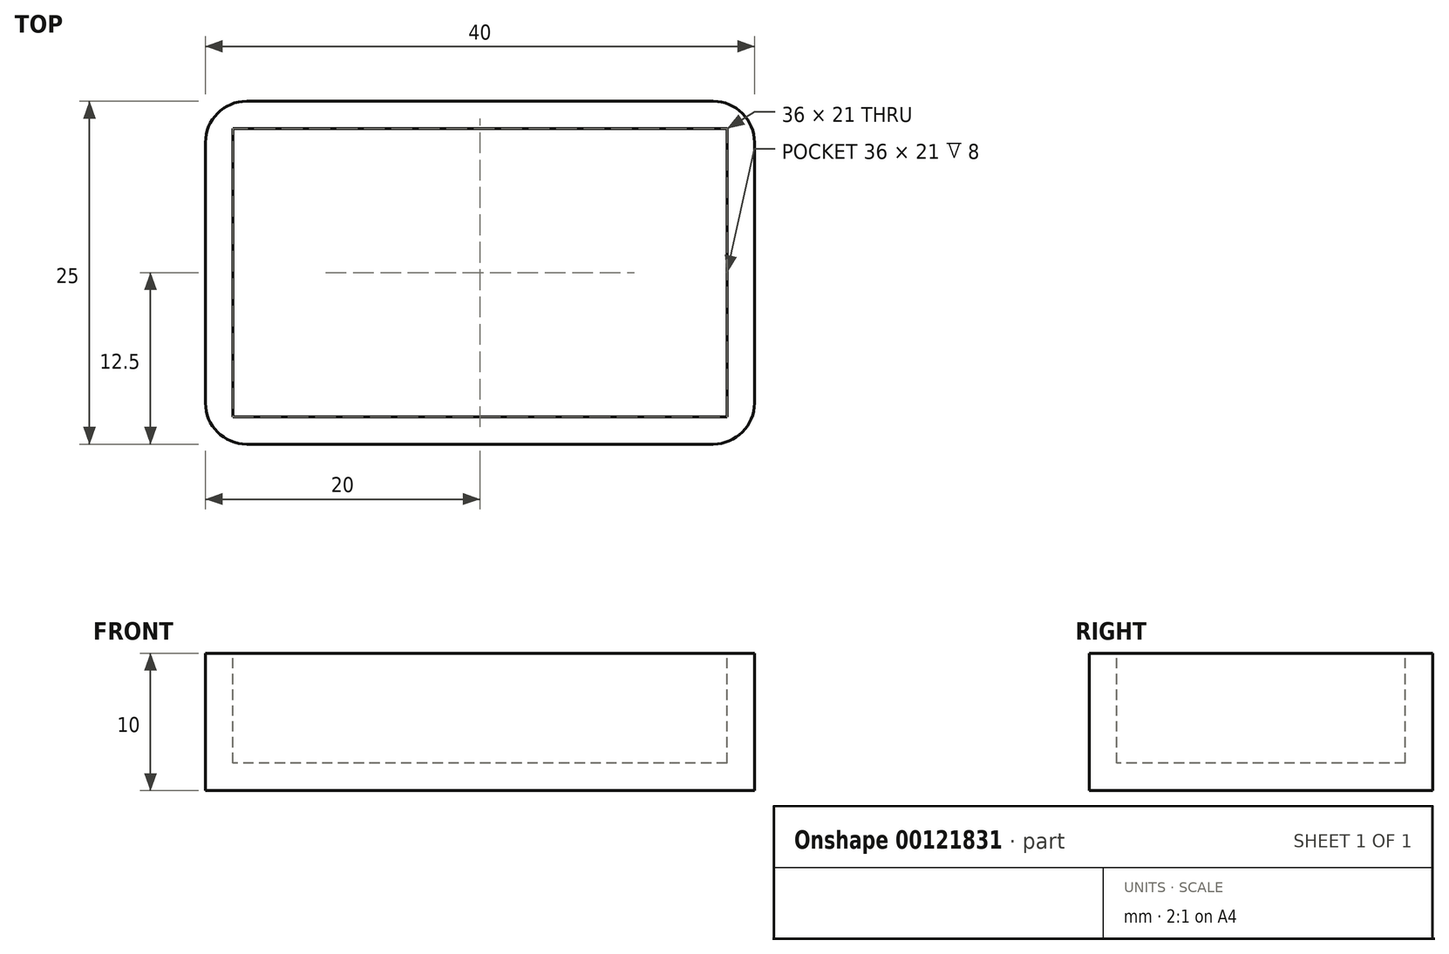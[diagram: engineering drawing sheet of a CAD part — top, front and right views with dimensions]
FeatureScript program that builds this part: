
annotation { "Feature Type Name" : "Feature", "Feature Type Description" : "" }
export const myFeature = defineFeature(function(context is Context, id is Id, definition is map)
    precondition{}
    {
        {
            var Q0;
            Q0=qCreatedBy(makeId("Top.planeOp"),FACE);
            var sketch = newSketch(context, id + "F0", { "sketchPlane" : qUnion([Q0])});
            skLineSegment(sketch, "E0.bottom", {"start": v(20, 12.5) * mm, "end": v(-20, 12.5) * mm});
            skLineSegment(sketch, "E0.top", {"start": v(20, -12.5) * mm, "end": v(-20, -12.5) * mm});
            skLineSegment(sketch, "E0.left", {"start": v(20, 12.5) * mm, "end": v(20, -12.5) * mm});
            skLineSegment(sketch, "E0.right", {"start": v(-20, 12.5) * mm, "end": v(-20, -12.5) * mm});
            skPoint(sketch, "E0.middle", {"position": v(0, 0) * mm});
            skSolve(sketch);
        }
        {
            var Q0;
            Q0=makeQuery(id+"F0.imprint","IMPRINT",FACE,{"disambiguationData":[TD([[makeQuery(id+"F0.imprint","IMPRINT",EDGE,{"derivedFrom":sQuery(id+"F0.wireOp",EDGE,"E0.bottom")}),1.0]])]});
            extrude(context, id + "F1", {"entities" : qUnion([Q0]), "depth" : 10 * mm});
        }
        {
            var Q0;
            Q0=makeQuery(id+"F1.opExtrude","CAP_FACE",FACE,{"disambiguationData":[OSD([sQuery(id+"F0.wireOp",EDGE,"E0.bottom"),sQuery(id+"F0.wireOp",EDGE,"E0.top"),sQuery(id+"F0.wireOp",EDGE,"E0.left"),sQuery(id+"F0.wireOp",EDGE,"E0.right")])],"isStart":false});
            var sketch = newSketch(context, id + "F2", { "sketchPlane" : qUnion([Q0])});
            skLineSegment(sketch, "E1.bottom", {"start": v(18, 10.5) * mm, "end": v(-18, 10.5) * mm});
            skLineSegment(sketch, "E1.top", {"start": v(18, -10.5) * mm, "end": v(-18, -10.5) * mm});
            skLineSegment(sketch, "E1.left", {"start": v(18, 10.5) * mm, "end": v(18, -10.5) * mm});
            skLineSegment(sketch, "E1.right", {"start": v(-18, 10.5) * mm, "end": v(-18, -10.5) * mm});
            skPoint(sketch, "E1.middle", {"position": v(0, 0) * mm});
            skSolve(sketch);
        }
        {
            var Q0;
            Q0=makeQuery(id+"F2.imprint","IMPRINT",FACE,{"disambiguationData":[TD([[makeQuery(id+"F2.imprint","IMPRINT",EDGE,{"derivedFrom":sQuery(id+"F2.wireOp",EDGE,"E1.bottom")}),1.0]])]});
            extrude(context, id + "F3", {"entities" : qUnion([Q0]), "operationType" : NewBodyOperationType.REMOVE, "oppositeDirection" : true, "depth" : 8 * mm});
        }
        {
            var Q0;
            Q0=makeQuery(id+"F1.opExtrude","SWEPT_EDGE",EDGE,{"disambiguationData":[OSD([sQuery(id+"F0.wireOp",EDGE,"E0.top"),sQuery(id+"F0.wireOp",EDGE,"E0.right")])]});
            var Q1;
            Q1=makeQuery(id+"F1.opExtrude","SWEPT_EDGE",EDGE,{"disambiguationData":[OSD([sQuery(id+"F0.wireOp",EDGE,"E0.top"),sQuery(id+"F0.wireOp",EDGE,"E0.left")])]});
            var Q2;
            Q2=makeQuery(id+"F1.opExtrude","SWEPT_EDGE",EDGE,{"disambiguationData":[OSD([sQuery(id+"F0.wireOp",EDGE,"E0.bottom"),sQuery(id+"F0.wireOp",EDGE,"E0.left")])]});
            var Q3;
            Q3=makeQuery(id+"F1.opExtrude","SWEPT_EDGE",EDGE,{"disambiguationData":[OSD([sQuery(id+"F0.wireOp",EDGE,"E0.bottom"),sQuery(id+"F0.wireOp",EDGE,"E0.right")])]});
            fillet(context, id + "F4", {"entities" : qUnion([Q0, Q1, Q2, Q3]), "radius" : 3 * mm, "tangentPropagation" : true, "allowEdgeOverflow" : false});
        }
    });
